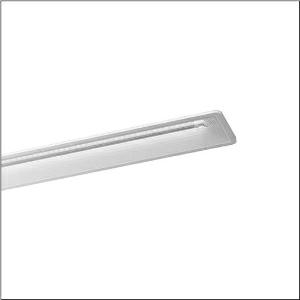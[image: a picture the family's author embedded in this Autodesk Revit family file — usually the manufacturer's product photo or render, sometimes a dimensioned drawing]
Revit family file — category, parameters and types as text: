
# Revit family: taris_r__21_5mt117d03wd_677e
name_source: partatom
category: Lighting Fixtures
units: mm (PartAtom-declared; Revit-internal decimal feet)

## family parameters
Cut with Voids When Loaded = No
Host = Face
Light Source = No
Part Type = Normal
Room Calculation Point = No
Round Connector Dimension = Use Diameter
Shared = No

## types (1)
- --- (1 x LED, 5700 lm, 35.9 W, 3000K)
    Apparent Load = 36 VA
    CIE Flux Codes = 73 96 99 100 100
    Color Rendering = 80
    Color Temperature = 3000K
    Default Elevation = 1800 mm
    Description = Taris® 21, office luminaire, primary anti-glare with micro louvre, primary optical cover: axial lens, of PMMA, structured, CAT 2 (L<= 1500cd/m²), light emission: direct distribution, primary light characteristic: symmetric, installation type: recessed, LED, rated luminous flux: 5.700lm, luminous efficacy: 159lm/W, light colour: 830, colour temperature: 3000K, control gear: ECG DALI, with terminal, 5-pole, mains connection: 230V, AC, 50Hz, rated input power: 36W, housing, luminaire housing, of plastic, pure white, length: 1.530mm, width: 150mm, height: 76mm, recess depth: 106mm, protection rating (complete): IP20, insulation class (complete): insulation class I (protective earthing), certification: CE, ENEC, VDE, protection symbol: F, impact resistance: IK02, permissible operating ambient temperature: 0..+35°C, standard: EN 50419, packaging unit: 1 piece
    Height = 0 mm  [stored 0 ft]
    Lamp = 1 x LED
    Lamp Light Flux = 5700 lm
    Lamp Power = 35.9 W
    Lamp count = 1
    Length = 1524 mm  [stored 5 ft]
    Luminous efficacy = 159 lm/W
    Manufacturer = Siteco
    ModVariant = No
    Model = 5MT117D03WD
    Mounting Place = Ceiling
    Mounting Type = Recessed
    Number of Poles = 1
    OnlyDefault = Yes
    Power Factor = 1
    Product Name = Taris® 21
    Product group = office luminaire | ceiling recessed
    ProductGroupID = 401
    Protection Class = Protection class I
    Protection Degree = IP 20
    RLX_Detail_Level = 1
    RLX_Emergency_Light_Flux = 0 lm
    RLX_Emergency_Type = 0
    RLX_Emergency_Type_DB = No
    RlxData = <blob elided: 30473 chars, md5=f479780b>
    Socket = socket
    Standby Power = 0 W
    System Light Flux = 5700 lm
    System Power = 36 W
    Type Comments = factory setting: luminous flux: 100 % | dim-lin: 254 | 200 mA
    Type Image = l_1004723.jpg
    URL = http://relux.com
    VarID = @adj_136975
    Voltage = 0 V
    Weight = 0.00 kg
    Width = 144 mm

note: [stored X ft] marks values corroborated as IEEE doubles in the binary element streams (Revit-internal decimal feet)

## geometry (parser evidence)
native form markers: Blend x4, Sweep x10
no freeform markers — native parametric forms only
